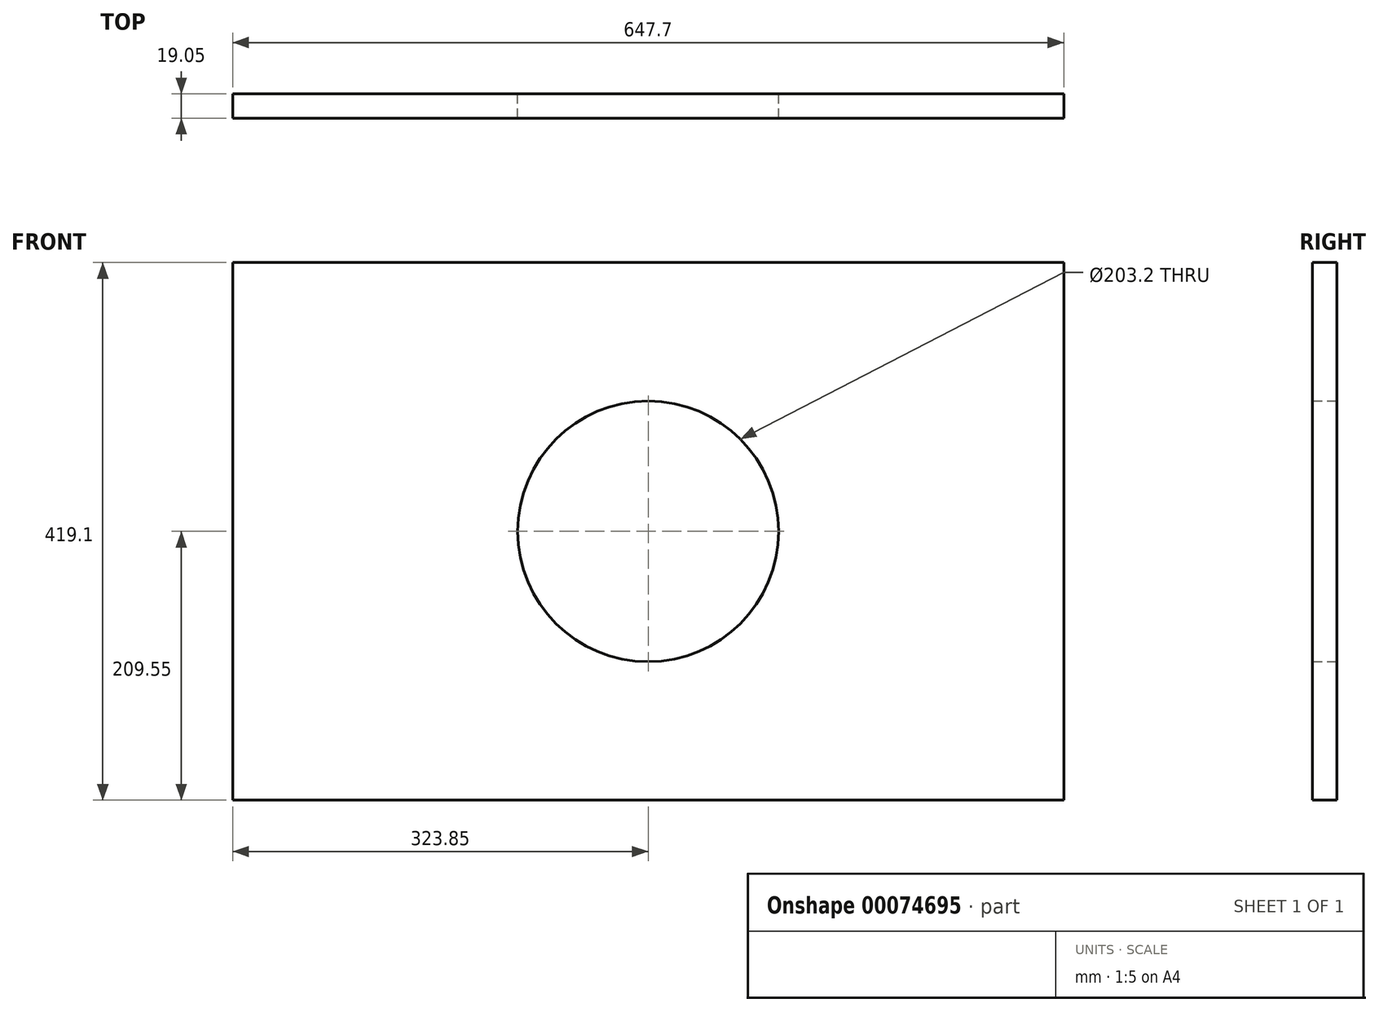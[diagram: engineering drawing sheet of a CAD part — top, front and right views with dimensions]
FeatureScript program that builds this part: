
annotation { "Feature Type Name" : "Feature", "Feature Type Description" : "" }
export const myFeature = defineFeature(function(context is Context, id is Id, definition is map)
    precondition{}
    {
        {
            var Q0;
            Q0=qCreatedBy(makeId("Front.planeOp"),FACE);
            var sketch = newSketch(context, id + "F0", { "sketchPlane" : qUnion([Q0])});
            skLineSegment(sketch, "E0.bottom", {"start": v(-317.5, 203.2) * mm, "end": v(317.5, 203.2) * mm, "construction": true});
            skLineSegment(sketch, "E0.top", {"start": v(-317.5, -203.2) * mm, "end": v(317.5, -203.2) * mm, "construction": true});
            skLineSegment(sketch, "E0.left", {"start": v(-317.5, 203.2) * mm, "end": v(-317.5, -203.2) * mm, "construction": true});
            skLineSegment(sketch, "E0.right", {"start": v(317.5, 203.2) * mm, "end": v(317.5, -203.2) * mm, "construction": true});
            skLineSegment(sketch, "E1.0", {"start": v(-323.85, -209.55) * mm, "end": v(323.85, -209.55) * mm});
            skLineSegment(sketch, "E1.1", {"start": v(-323.85, 209.55) * mm, "end": v(-323.85, -209.55) * mm});
            skLineSegment(sketch, "E1.2", {"start": v(-323.85, 209.55) * mm, "end": v(323.85, 209.55) * mm});
            skLineSegment(sketch, "E1.3", {"start": v(323.85, 209.55) * mm, "end": v(323.85, -209.55) * mm});
            skLineSegment(sketch, "E2", {"start": v(-323.85, 0) * mm, "end": v(0, 0) * mm, "construction": true});
            skLineSegment(sketch, "E3", {"start": v(0, 0) * mm, "end": v(0, -209.55) * mm, "construction": true});
            skCircle(sketch, "E4", {"center": v(0, 0) * mm, "radius": 101.6 * mm});
            skSolve(sketch);
        }
        {
            var Q0;
            Q0 = qSketchRegion(id + "F0", true);
            extrude(context, id + "F1", {"entities" : qUnion([Q0]), "depth" : 19.05 * mm});
        }
    });
